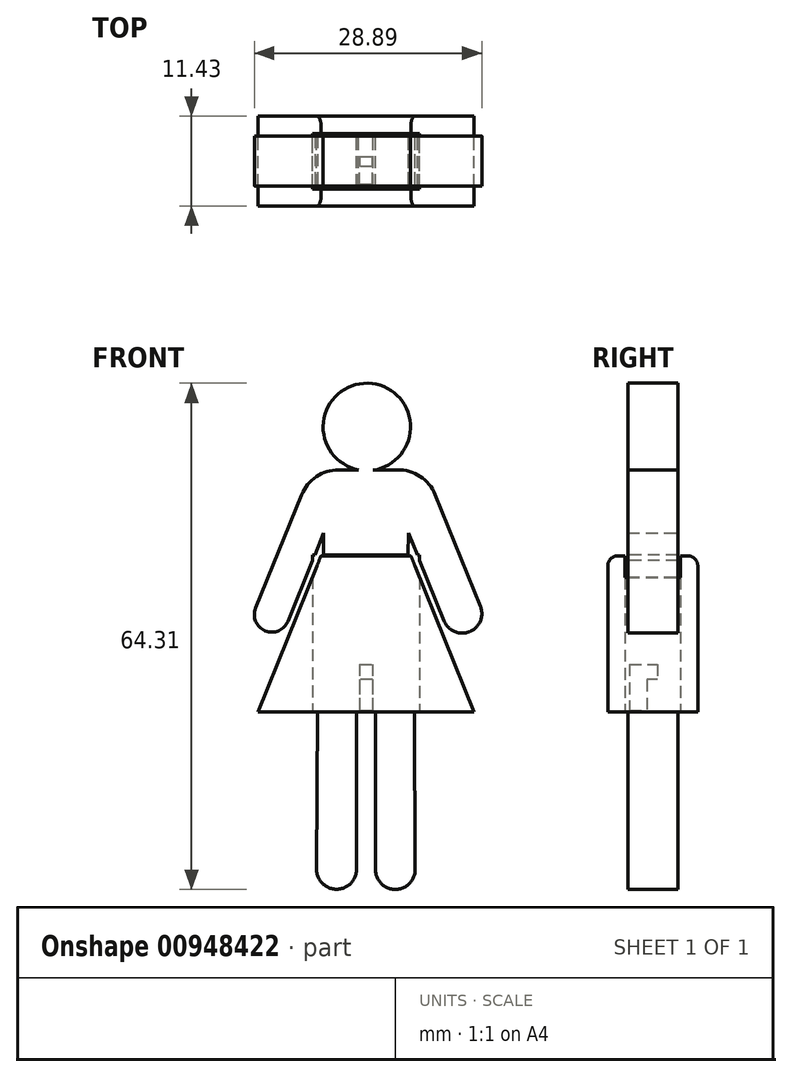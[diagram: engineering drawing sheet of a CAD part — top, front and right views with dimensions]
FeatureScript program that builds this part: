
annotation { "Feature Type Name" : "Feature", "Feature Type Description" : "" }
export const myFeature = defineFeature(function(context is Context, id is Id, definition is map)
    precondition{}
    {
        {
            var Q0;
            Q0=qCreatedBy(makeId("Front.planeOp"),FACE);
            var sketch = newSketch(context, id + "F0", { "sketchPlane" : qUnion([Q0])});
            skLineSegment(sketch, "E0", {"start": v(0, 57.53) * mm, "end": v(-13.75, 23.6) * mm});
            skLineSegment(sketch, "E1", {"start": v(-13.75, 23.6) * mm, "end": v(13.75, 23.6) * mm});
            skLineSegment(sketch, "E2", {"start": v(13.75, 23.6) * mm, "end": v(0, 57.53) * mm});
            skSolve(sketch);
        }
        {
            var Q0;
            Q0=qCreatedBy(makeId("Front.planeOp"),FACE);
            var sketch = newSketch(context, id + "F1", { "sketchPlane" : qUnion([Q0])});
            skLineSegment(sketch, "E3", {"start": v(5.38, 46.34) * mm, "end": v(9.92, 35.14) * mm});
            skLineSegment(sketch, "E4", {"start": v(9.92, 35.14) * mm, "end": v(14.53, 37) * mm});
            skLineSegment(sketch, "E5", {"start": v(14.53, 37) * mm, "end": v(7.48, 54.4) * mm});
            skLineSegment(sketch, "E6", {"start": v(0.4, 46.34) * mm, "end": v(5.38, 46.34) * mm});
            skLineSegment(sketch, "E7", {"start": v(-6.9, 54.33) * mm, "end": v(-14.02, 36.76) * mm});
            skLineSegment(sketch, "E8", {"start": v(-14.02, 36.76) * mm, "end": v(-9.93, 35.1) * mm});
            skLineSegment(sketch, "E9", {"start": v(-9.93, 35.1) * mm, "end": v(-5.37, 46.34) * mm});
            skLineSegment(sketch, "E10", {"start": v(-5.37, 46.34) * mm, "end": v(0.4, 46.34) * mm});
            skArc(sketch, "E11", {"start": v(-14.02, 36.76) * mm, "mid": v(-12.8, 33.88) * mm, "end": v(-9.93, 35.1) * mm});
            skArc(sketch, "E12", {"start": v(9.92, 35.14) * mm, "mid": v(13.16, 33.77) * mm, "end": v(14.53, 37) * mm});
            skLineSegment(sketch, "E13", {"start": v(-5.37, 46.34) * mm, "end": v(-5.4, 30.2) * mm});
            skLineSegment(sketch, "E14", {"start": v(-5.4, 30.2) * mm, "end": v(-6.18, 23.6) * mm});
            skLineSegment(sketch, "E15", {"start": v(6.18, 23.6) * mm, "end": v(4.9, 30.2) * mm});
            skLineSegment(sketch, "E16", {"start": v(4.9, 30.2) * mm, "end": v(5.38, 46.34) * mm});
            skLineSegment(sketch, "E17", {"start": v(-5.4, 30.2) * mm, "end": v(4.9, 30.2) * mm});
            skLineSegment(sketch, "E18", {"start": v(-6.18, 23.6) * mm, "end": v(-1.2, 23.6) * mm});
            skLineSegment(sketch, "E19", {"start": v(-1.2, 23.6) * mm, "end": v(-1.2, 30.16) * mm});
            skLineSegment(sketch, "E20", {"start": v(-1.2, 30.16) * mm, "end": v(1.2, 30.16) * mm});
            skLineSegment(sketch, "E21", {"start": v(1.2, 30.16) * mm, "end": v(1.2, 23.55) * mm});
            skLineSegment(sketch, "E22", {"start": v(1.2, 23.55) * mm, "end": v(6.18, 23.6) * mm});
            skLineSegment(sketch, "E23", {"start": v(-6.9, 54.33) * mm, "end": v(-0.95, 54.33) * mm});
            skLineSegment(sketch, "E24", {"start": v(-0.95, 54.33) * mm, "end": v(-0.95, 55.77) * mm});
            skLineSegment(sketch, "E25", {"start": v(-0.95, 55.77) * mm, "end": v(0.9, 55.77) * mm});
            skLineSegment(sketch, "E26", {"start": v(0.9, 55.77) * mm, "end": v(0.9, 54.3) * mm});
            skLineSegment(sketch, "E27", {"start": v(0.9, 54.3) * mm, "end": v(7.48, 54.4) * mm});
            skArc(sketch, "E28", {"start": v(0.9, 54.3) * mm, "mid": v(0.23, 65.34) * mm, "end": v(-0.95, 54.33) * mm});
            skLineSegment(sketch, "E29", {"start": v(-1.2, 23.6) * mm, "end": v(-1.2, 3.62) * mm});
            skLineSegment(sketch, "E30", {"start": v(-1.2, 3.62) * mm, "end": v(-6.3, 3.62) * mm});
            skLineSegment(sketch, "E31", {"start": v(-6.3, 3.62) * mm, "end": v(-6.18, 23.6) * mm});
            skLineSegment(sketch, "E32", {"start": v(1.2, 23.55) * mm, "end": v(1.2, 3.57) * mm});
            skLineSegment(sketch, "E33", {"start": v(1.2, 3.57) * mm, "end": v(6.25, 3.57) * mm});
            skLineSegment(sketch, "E34", {"start": v(6.25, 3.57) * mm, "end": v(6.18, 23.6) * mm});
            skArc(sketch, "E35", {"start": v(-6.3, 3.62) * mm, "mid": v(-3.75, 1.06) * mm, "end": v(-1.2, 3.62) * mm});
            skArc(sketch, "E36", {"start": v(1.2, 3.57) * mm, "mid": v(3.72, 1.03) * mm, "end": v(6.25, 3.57) * mm});
            skSolve(sketch);
        }
        {
            var Q0;
            Q0 = qSketchRegion(id + "F1", true);
            extrude(context, id + "F2", {"entities" : qUnion([Q0]), "depth" : 6.35 * mm, "offsetDistance" : 25.4 * mm});
        }
        {
            var Q0;
            Q0=makeQuery(id+"F2.opExtrude","SWEPT_EDGE",EDGE,{"disambiguationData":[OSD([sQuery(id+"F1.wireOp",EDGE,"E7"),sQuery(id+"F1.wireOp",EDGE,"E23")])]});
            var Q1;
            Q1=makeQuery(id+"F2.opExtrude","SWEPT_EDGE",EDGE,{"disambiguationData":[OSD([sQuery(id+"F1.wireOp",EDGE,"E5"),sQuery(id+"F1.wireOp",EDGE,"E27")])]});
            fillet(context, id + "F3", {"entities" : qUnion([Q0, Q1]), "radius" : 5.08 * mm, "tangentPropagation" : true, "allowEdgeOverflow" : false});
        }
        {
            var Q0;
            Q0=qCreatedBy(makeId("Front.planeOp"),FACE);
            var sketch = newSketch(context, id + "F4", { "sketchPlane" : qUnion([Q0])});
            skLineSegment(sketch, "E37", {"start": v(-13.73, 23.6) * mm, "end": v(13.74, 23.6) * mm});
            skLineSegment(sketch, "E38", {"start": v(13.74, 23.6) * mm, "end": v(5.7, 43.4) * mm});
            skLineSegment(sketch, "E39", {"start": v(5.7, 43.4) * mm, "end": v(-5.72, 43.4) * mm});
            skLineSegment(sketch, "E40", {"start": v(-5.72, 43.4) * mm, "end": v(-13.73, 23.6) * mm});
            skSolve(sketch);
        }
        {
            var Q0;
            Q0=makeQuery(id+"F4.imprint","IMPRINT",FACE,{"disambiguationData":[TD([[makeQuery(id+"F4.imprint","IMPRINT",EDGE,{"derivedFrom":sQuery(id+"F4.wireOp",EDGE,"E37")}),1.0]])]});
            extrude(context, id + "F5", {"entities" : qUnion([Q0]), "depth" : 8.9 * mm, "offsetDistance" : 25.4 * mm, "hasSecondDirection" : true, "secondDirectionOppositeDirection" : true, "secondDirectionDepth" : 2.54 * mm});
        }
        {
            var Q0;
            Q0=makeQuery(id+"F5.opExtrude","CAP_EDGE",EDGE,{"disambiguationData":[OSD([sQuery(id+"F4.wireOp",EDGE,"E39")])],"isStart":true});
            var Q1;
            Q1=makeQuery(id+"F5.opExtrude","CAP_EDGE",EDGE,{"disambiguationData":[OSD([sQuery(id+"F4.wireOp",EDGE,"E39")])],"isStart":false});
            fillet(context, id + "F6", {"entities" : qUnion([Q0, Q1]), "radius" : 1.27 * mm, "tangentPropagation" : true, "allowEdgeOverflow" : false});
        }
        {
            var Q0;
            Q0=makeQuery(id+"F5.opExtrude","SWEPT_FACE",FACE,{"disambiguationData":[OSD([sQuery(id+"F4.wireOp",EDGE,"E37")])]});
            var sketch = newSketch(context, id + "F7", { "sketchPlane" : qUnion([Q0])});
            skLineSegment(sketch, "E41.bottom", {"start": v(-6.8, 6.74) * mm, "end": v(6.8, 6.74) * mm});
            skLineSegment(sketch, "E41.top", {"start": v(-6.8, -0.33) * mm, "end": v(6.8, -0.33) * mm});
            skLineSegment(sketch, "E41.left", {"start": v(-6.8, 6.74) * mm, "end": v(-6.8, -0.33) * mm});
            skLineSegment(sketch, "E41.right", {"start": v(6.8, 6.74) * mm, "end": v(6.8, -0.33) * mm});
            skSolve(sketch);
        }
        {
            var Q0;
            Q0=makeQuery(id+"F7.imprint","IMPRINT",FACE,{"disambiguationData":[TD([[makeQuery(id+"F7.imprint","IMPRINT",EDGE,{"derivedFrom":sQuery(id+"F7.wireOp",EDGE,"E41.bottom")}),-1.0]])]});
            extrude(context, id + "F8", {"entities" : qUnion([Q0]), "operationType" : NewBodyOperationType.REMOVE, "oppositeDirection" : true, "depth" : 19.94 * mm, "offsetDistance" : 25.4 * mm});
        }
        {
            var Q0;
            Q0=qCreatedBy(makeId("Front.planeOp"),FACE);
            cPlane(context, id + "F9", {"entities" : qUnion([Q0]), "cplaneType" : CPlaneType.OFFSET, "offset" : 3.9 * mm, "width" : 152.4 * mm, "height" : 152.4 * mm});
        }
        {
            var Q0;
            Q0=qCreatedBy(id+"F9.planeOp",FACE);
            var sketch = newSketch(context, id + "F10", { "sketchPlane" : qUnion([Q0])});
            skLineSegment(sketch, "E42.bottom", {"start": v(-0.82, 29.62) * mm, "end": v(0.82, 29.62) * mm});
            skLineSegment(sketch, "E42.top", {"start": v(-0.82, 23.78) * mm, "end": v(0.82, 23.78) * mm});
            skLineSegment(sketch, "E42.left", {"start": v(-0.82, 29.62) * mm, "end": v(-0.82, 23.78) * mm});
            skLineSegment(sketch, "E42.right", {"start": v(0.82, 29.62) * mm, "end": v(0.82, 23.78) * mm});
            skSolve(sketch);
        }
        {
            var Q0;
            Q0=makeQuery(id+"F10.imprint","IMPRINT",FACE,{"disambiguationData":[TD([[makeQuery(id+"F10.imprint","IMPRINT",EDGE,{"derivedFrom":sQuery(id+"F10.wireOp",EDGE,"E42.bottom")}),-1.0]])]});
            extrude(context, id + "F11", {"entities" : qUnion([Q0]), "depth" : 2.23 * mm, "offsetDistance" : 25.4 * mm});
        }
        {
            var Q0;
            Q0=makeQuery(id+"F11.opExtrude","CAP_FACE",FACE,{"disambiguationData":[OSD([sQuery(id+"F10.wireOp",EDGE,"E42.bottom"),sQuery(id+"F10.wireOp",EDGE,"E42.top"),sQuery(id+"F10.wireOp",EDGE,"E42.left"),sQuery(id+"F10.wireOp",EDGE,"E42.right")])],"isStart":true});
            var sketch = newSketch(context, id + "F12", { "sketchPlane" : qUnion([Q0])});
            skLineSegment(sketch, "E43.bottom", {"start": v(-0.82, 29.62) * mm, "end": v(0.82, 29.62) * mm});
            skLineSegment(sketch, "E43.top", {"start": v(-0.82, 27.68) * mm, "end": v(0.82, 27.68) * mm});
            skLineSegment(sketch, "E43.left", {"start": v(-0.82, 29.62) * mm, "end": v(-0.82, 27.68) * mm});
            skLineSegment(sketch, "E43.right", {"start": v(0.82, 29.62) * mm, "end": v(0.82, 27.68) * mm});
            skSolve(sketch);
        }
        {
            var Q0;
            Q0=makeQuery(id+"F12.imprint","IMPRINT",FACE,{"disambiguationData":[TD([[makeQuery(id+"F12.imprint","IMPRINT",EDGE,{"derivedFrom":sQuery(id+"F12.wireOp",EDGE,"E43.bottom")}),1.0]])]});
            extrude(context, id + "F13", {"entities" : qUnion([Q0]), "operationType" : NewBodyOperationType.ADD, "depth" : 1.29 * mm, "offsetDistance" : 25.4 * mm});
        }
    });
